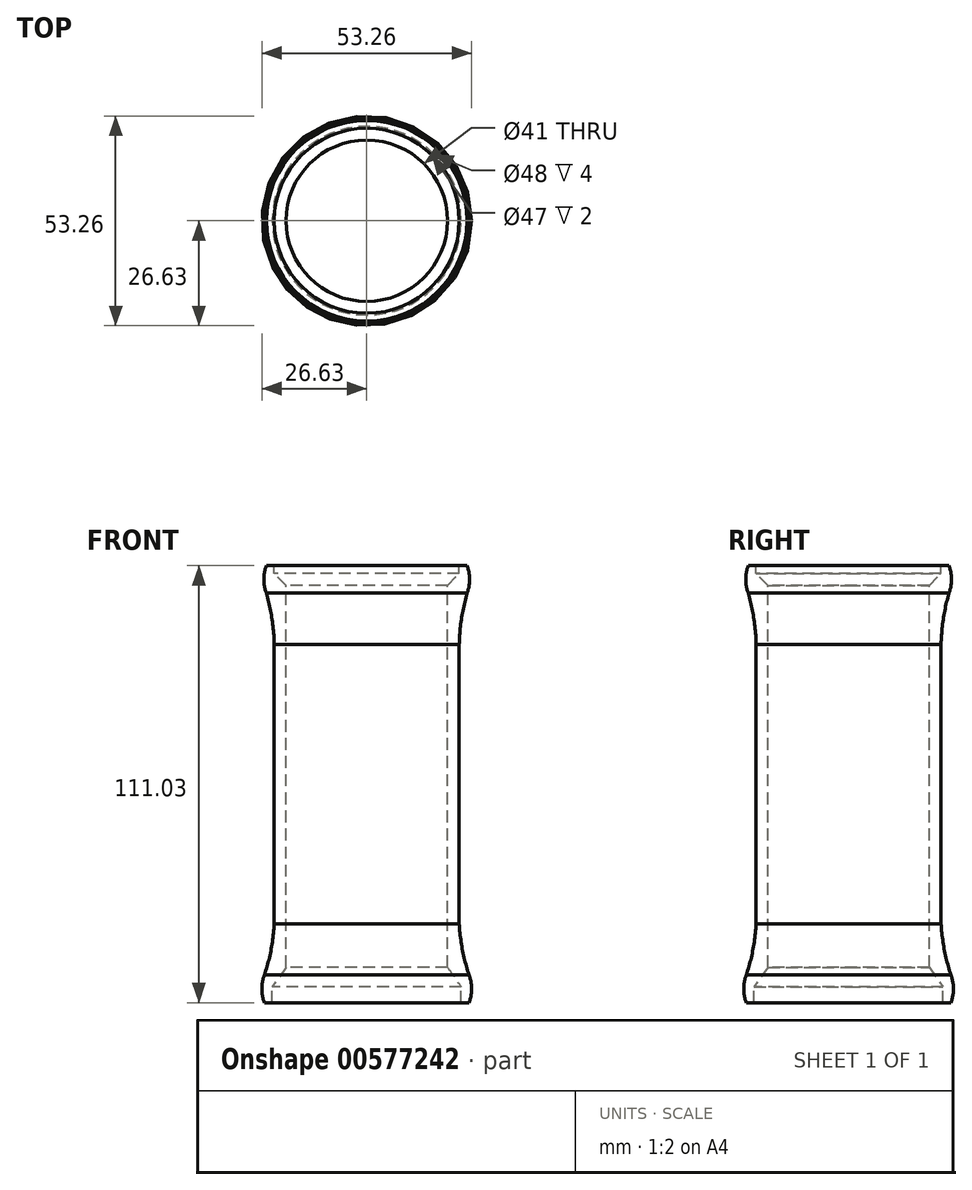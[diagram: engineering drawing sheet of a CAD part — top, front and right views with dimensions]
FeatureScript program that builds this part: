
annotation { "Feature Type Name" : "Feature", "Feature Type Description" : "" }
export const myFeature = defineFeature(function(context is Context, id is Id, definition is map)
    precondition{}
    {
        {
            var Q0;
            Q0=qCreatedBy(makeId("Front.planeOp"),FACE);
            var sketch = newSketch(context, id + "F0", { "sketchPlane" : qUnion([Q0])});
            skLineSegment(sketch, "E0", {"start": v(0, 0) * mm, "end": v(0, 49.5) * mm});
            skLineSegment(sketch, "E1", {"start": v(0, 49.5) * mm, "end": v(3, 52.5) * mm});
            skLineSegment(sketch, "E2", {"start": v(3, 52.5) * mm, "end": v(3, 54.5) * mm});
            skLineSegment(sketch, "E3", {"start": v(3, 54.5) * mm, "end": v(5, 54.5) * mm});
            skArc(sketch, "E4", {"start": v(5, 47.5) * mm, "mid": v(5.63, 51) * mm, "end": v(5, 54.5) * mm});
            skArc(sketch, "E5", {"start": v(5, 47.5) * mm, "mid": v(3.57, 41.07) * mm, "end": v(3, 34.5) * mm});
            skLineSegment(sketch, "E6", {"start": v(3, 34.5) * mm, "end": v(3, 0) * mm});
            skLineSegment(sketch, "E7", {"start": v(0, 0) * mm, "end": v(0, -47.5) * mm});
            skLineSegment(sketch, "E8", {"start": v(0, -47.5) * mm, "end": v(3.5, -52.53) * mm});
            skLineSegment(sketch, "E9", {"start": v(3.5, -52.53) * mm, "end": v(3.5, -56.53) * mm});
            skLineSegment(sketch, "E10", {"start": v(3.5, -56.53) * mm, "end": v(3.5, -56.53) * mm});
            skLineSegment(sketch, "E11", {"start": v(3.5, -56.53) * mm, "end": v(5.5, -56.53) * mm});
            skArc(sketch, "E12", {"start": v(5.5, -56.53) * mm, "mid": v(6.13, -53.03) * mm, "end": v(5.5, -49.53) * mm});
            skArc(sketch, "E13", {"start": v(3, -36.53) * mm, "mid": v(3.82, -43.11) * mm, "end": v(5.5, -49.53) * mm});
            skLineSegment(sketch, "E14", {"start": v(3, 0) * mm, "end": v(3, -36.53) * mm});
            skLineSegment(sketch, "E15", {"start": v(-20.5, 57.3) * mm, "end": v(-20.5, -55.17) * mm});
            skSolve(sketch);
        }
        {
            var Q0;
            Q0=makeQuery(id+"F0.imprint","IMPRINT",FACE,{"disambiguationData":[TD([[makeQuery(id+"F0.imprint","IMPRINT",EDGE,{"derivedFrom":sQuery(id+"F0.wireOp",EDGE,"E0")}),-1.0]])]});
            var Q1;
            Q1=sQuery(id+"F0.wireOp",EDGE,"E15");
            revolve(context, id + "F1", {"entities" : qUnion([Q0]), "axis" : qUnion([Q1]), "revolveType" : RevolveType.FULL});
        }
    });
